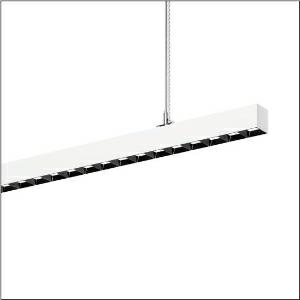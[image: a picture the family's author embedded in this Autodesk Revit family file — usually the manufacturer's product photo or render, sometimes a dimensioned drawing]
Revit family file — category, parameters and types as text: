
# Revit family: silica_r__21_51mx31dc3dwb_5f0e
name_source: partatom
category: Lighting Fixtures
units: mm (PartAtom-declared; Revit-internal decimal feet)

## family parameters
Cut with Voids When Loaded = No
Host = Face
Light Source = No
Part Type = Normal
Room Calculation Point = No
Round Connector Dimension = Use Diameter
Shared = No

## types (1)
- --- (1 x LED, 18230 lm, 113.3 W, 3000K)
    Apparent Load = 113 VA
    CIE Flux Codes = 87 99 100 59 100
    Color Rendering = 80
    Color Temperature = 3000K
    Default Elevation = 1800 mm
    Description = Silica® 21, office luminaire, primary light control with darklight reflector, of PMMA, black, CAT 2 (L<= 3000cd/m²), light emission: direct/indirect distribution, primary light characteristic: symmetric, installation type: suspended mounting, LED, rated luminous flux: 18.230lm, luminous efficacy: 161lm/W, light colour: 830, colour temperature: 3000K, with terminal, 3+2-pole, max. 2.5mm², mains connection: 220..240V, AC, 50/60Hz, rated input power: 113.3W, luminaire housing, of aluminium, traffic white (RAL 9016), length: 3.004mm, width: 53mm, height: 53mm, protection rating (complete): IP20, insulation class (complete): insulation class I (protective earthing), certification: CE, permissible operating ambient temperature: 0..+35°C, standard: EN 50419, packaging unit: 1 piece
    Height = 53 mm
    Lamp = 1 x LED
    Lamp Light Flux = 18230 lm
    Lamp Power = 113.3 W
    Lamp count = 1
    Length = 3004 mm
    Luminous efficacy = 161 lm/W
    Manufacturer = Siteco
    ModVariant = No
    Model = 51MX31DC3DWB
    Mounting Place = Ceiling
    Mounting Type = Pendant
    Number of Poles = 1
    OnlyDefault = Yes
    Power Factor = 1
    Product Name = Silica® 21
    Product group = office luminaire | ceiling pendant
    ProductGroupID = 905
    Protection Class = Protection class I
    Protection Degree = IP 20
    RLX_Detail_Level = 1
    RlxData = <blob elided: 64381 chars, md5=91b930de>
    Socket = socket
    Standby Power = 0 W
    System Light Flux = 18230 lm
    System Power = 113 W
    Type Comments = factory setting: luminous flux: 100 % | dim-lin: 254 | 392 mA
    Type Image = l_1251637.jpg
    URL = http://relux.com
    VarID = @adj_030245
    Voltage = 0 V
    Weight = 0.00 kg
    Width = 53 mm

## geometry (parser evidence)
native form markers: Blend x4, Sweep x11
no freeform markers — native parametric forms only
